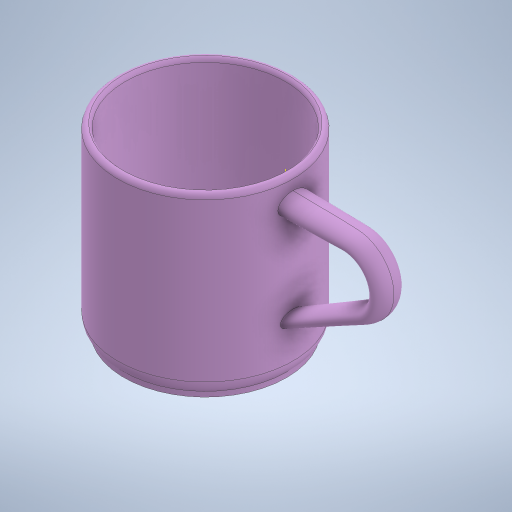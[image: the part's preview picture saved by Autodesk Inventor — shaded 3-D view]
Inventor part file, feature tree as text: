
AUTODESK INVENTOR PART (.ipt)
format: ipt  version: 2024 (Build 280153000, 153)  size: 380,928 bytes
history: native  units: mm
features: sketch x13, other x4, plane x2, revolve x1, shell x1, loft x1, fillet x1, extrude x1
ambient origin geometry x8: Origin, YZ Plane, XZ Plane, XY Plane, X Axis, Y Axis, Z Axis, Center Point
bodies: Solid1 (feature_tree)
feature tree (24):
  other  "CrossSection1"
  revolve  "Revolution1"  [1 undecoded]
  shell  "Shell1"  Thickness=35.0mm
  sketch  "Sketch2"  dims[d3=65.0mm d4=90.0deg d5=3.0mm]
  sketch  "Sketch3"  dims[d6=0.5mm d7=2.0mm d8=0.0mm d9=20.0mm d11=25.0mm]
  sketch  "Sketch4"  dims[d14=12.0mm]
  other  "Work Point1"
  other  "Work Point2"
  sketch  "Sketch5"  dims[d15=4.0mm]
  other  "Work Point3"
  plane  "Work Plane2"
  sketch  "Sketch6"  dims[d16=6.0mm]
  plane  "Work Plane3"
  sketch  "Sketch7"  dims[d17=3.0mm]
  sketch  "Sketch8"  dims[d18=5.0mm]
  sketch  "3D Sketch1"
  sketch  "3D Sketch2"
  sketch  "3D Sketch3"
  sketch  "Sketch9"  dims[d19=0.0mm d20=90.0deg]
  loft  "Loft1"
  fillet  "Fillet1"  Radius=3.0mm
  extrude  "Extrusion1"  Depth=2.0mm
  sketch  "Sketch1"  dims[d0=32.5mm d1=70.0mm d2=35.0mm]
  sketch  "Sketch10"  dims[d21=0.0mm d22=90.0deg d23=0.0mm d24=90.0deg d25=2.0mm d26=65.0mm d27=62.0mm d28=2.0mm d29=0.0mm]
note: 1 required parameter value undecoded (feature->parameter linkage not recoverable at this tier; creation-order binding heuristic only, values carry confidence <= 0.55)
